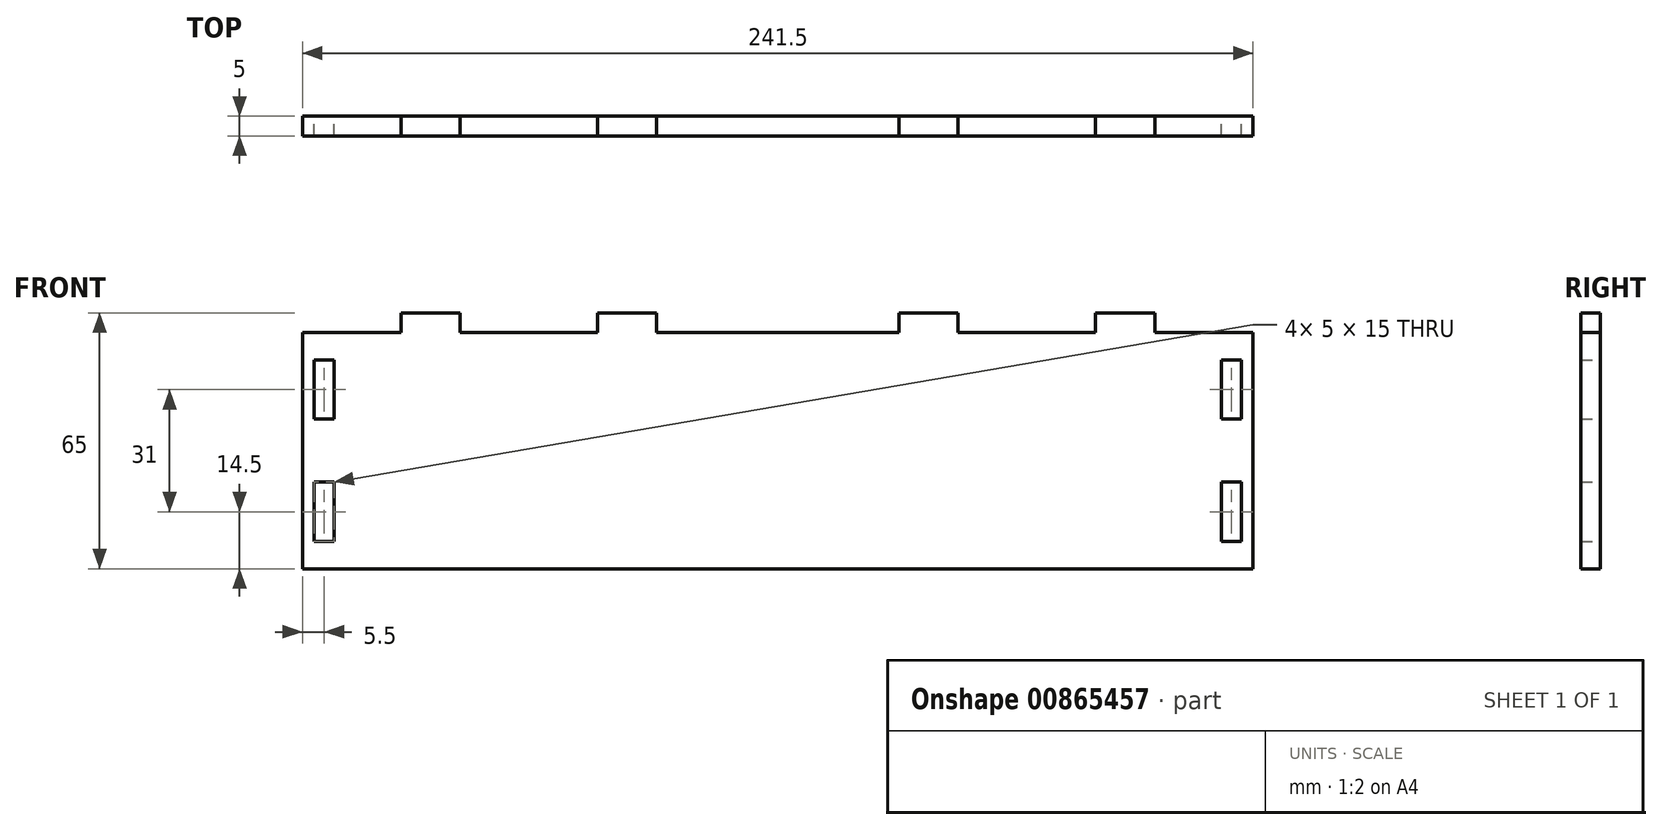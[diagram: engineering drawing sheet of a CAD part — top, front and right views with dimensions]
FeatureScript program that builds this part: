
annotation { "Feature Type Name" : "Feature", "Feature Type Description" : "" }
export const myFeature = defineFeature(function(context is Context, id is Id, definition is map)
    precondition{}
    {
        {
            var Q0;
            Q0=qCreatedBy(makeId("Front.planeOp"),FACE);
            var sketch = newSketch(context, id + "F0", { "sketchPlane" : qUnion([Q0])});
            skLineSegment(sketch, "E0.bottom", {"start": v(120.75, -30) * mm, "end": v(-120.75, -30) * mm});
            skLineSegment(sketch, "E0.top", {"start": v(120.75, 30) * mm, "end": v(-120.75, 30) * mm});
            skLineSegment(sketch, "E0.left", {"start": v(120.75, -30) * mm, "end": v(120.75, 30) * mm});
            skLineSegment(sketch, "E0.right", {"start": v(-120.75, -30) * mm, "end": v(-120.75, 30) * mm});
            skPoint(sketch, "E0.middle", {"position": v(0, 0) * mm});
            skLineSegment(sketch, "E1", {"start": v(-95.75, 30) * mm, "end": v(-95.75, 35) * mm});
            skLineSegment(sketch, "E2", {"start": v(-95.75, 35) * mm, "end": v(-80.75, 35) * mm});
            skLineSegment(sketch, "E3", {"start": v(-80.75, 35) * mm, "end": v(-80.75, 30) * mm});
            skSolve(sketch);
        }
        {
            var Q0;
            Q0=qCreatedBy(makeId("Front.planeOp"),FACE);
            var sketch = newSketch(context, id + "F1", { "sketchPlane" : qUnion([Q0])});
            skLineSegment(sketch, "E4.bottom", {"start": v(120.75, -30) * mm, "end": v(-120.75, -30) * mm});
            skLineSegment(sketch, "E4.top", {"start": v(120.75, 30) * mm, "end": v(-30.75, 30) * mm});
            skLineSegment(sketch, "E4.left", {"start": v(120.75, -30) * mm, "end": v(120.75, 30) * mm});
            skLineSegment(sketch, "E4.right", {"start": v(-120.75, -30) * mm, "end": v(-120.75, 30) * mm});
            skPoint(sketch, "E4.middle", {"position": v(0, 0) * mm});
            skLineSegment(sketch, "E5", {"start": v(-95.75, 30) * mm, "end": v(-95.75, 35) * mm});
            skLineSegment(sketch, "E6", {"start": v(-95.75, 35) * mm, "end": v(-80.75, 35) * mm});
            skLineSegment(sketch, "E7", {"start": v(-80.75, 35) * mm, "end": v(-80.75, 30) * mm});
            skLineSegment(sketch, "E8", {"start": v(-45.75, 30) * mm, "end": v(-45.75, 35) * mm});
            skLineSegment(sketch, "E9", {"start": v(-45.75, 35) * mm, "end": v(-30.75, 35) * mm});
            skLineSegment(sketch, "E10", {"start": v(-30.75, 35) * mm, "end": v(-30.75, 30) * mm});
            skLineSegment(sketch, "E11.trimOffspring", {"start": v(-95.75, 30) * mm, "end": v(-120.75, 30) * mm});
            skLineSegment(sketch, "E12.trimOffspring", {"start": v(-45.75, 30) * mm, "end": v(-80.75, 30) * mm});
            skLineSegment(sketch, "E13.MirrorCS", {"start": v(45.75, 35) * mm, "end": v(30.75, 35) * mm});
            skLineSegment(sketch, "E14.MirrorCS", {"start": v(45.75, 30) * mm, "end": v(45.75, 35) * mm});
            skLineSegment(sketch, "E15.MirrorCS", {"start": v(30.75, 35) * mm, "end": v(30.75, 30) * mm});
            skLineSegment(sketch, "E16.MirrorCS", {"start": v(80.75, 35) * mm, "end": v(80.75, 30) * mm});
            skLineSegment(sketch, "E17.MirrorCS", {"start": v(95.75, 30) * mm, "end": v(95.75, 35) * mm});
            skLineSegment(sketch, "E18.MirrorCS", {"start": v(95.75, 35) * mm, "end": v(80.75, 35) * mm});
            skLineSegment(sketch, "E19.bottom", {"start": v(-112.75, 8) * mm, "end": v(-117.75, 8) * mm});
            skLineSegment(sketch, "E19.top", {"start": v(-112.75, 23) * mm, "end": v(-117.75, 23) * mm});
            skLineSegment(sketch, "E19.left", {"start": v(-112.75, 8) * mm, "end": v(-112.75, 23) * mm});
            skLineSegment(sketch, "E19.right", {"start": v(-117.75, 8) * mm, "end": v(-117.75, 23) * mm});
            skPoint(sketch, "E19.middle", {"position": v(-115.25, 15.5) * mm});
            skLineSegment(sketch, "E20.MirrorCS", {"start": v(-117.75, -8) * mm, "end": v(-117.75, -23) * mm});
            skLineSegment(sketch, "E21.MirrorCS", {"start": v(-112.75, -8) * mm, "end": v(-112.75, -23) * mm});
            skLineSegment(sketch, "E22.MirrorCS", {"start": v(-112.75, -23) * mm, "end": v(-117.75, -23) * mm});
            skLineSegment(sketch, "E23.MirrorCS", {"start": v(-112.75, -8) * mm, "end": v(-117.75, -8) * mm});
            skLineSegment(sketch, "E24.MirrorCS", {"start": v(112.75, 8) * mm, "end": v(112.75, 23) * mm});
            skLineSegment(sketch, "E25.MirrorCS", {"start": v(117.75, 8) * mm, "end": v(117.75, 23) * mm});
            skLineSegment(sketch, "E26.MirrorCS", {"start": v(112.75, 23) * mm, "end": v(117.75, 23) * mm});
            skLineSegment(sketch, "E27.MirrorCS", {"start": v(112.75, 8) * mm, "end": v(117.75, 8) * mm});
            skLineSegment(sketch, "E28.MirrorCS", {"start": v(112.75, -8) * mm, "end": v(117.75, -8) * mm});
            skLineSegment(sketch, "E29.MirrorCS", {"start": v(112.75, -8) * mm, "end": v(112.75, -23) * mm});
            skLineSegment(sketch, "E30.MirrorCS", {"start": v(117.75, -8) * mm, "end": v(117.75, -23) * mm});
            skLineSegment(sketch, "E31.MirrorCS", {"start": v(112.75, -23) * mm, "end": v(117.75, -23) * mm});
            skPoint(sketch, "E32.middle", {"position": v(80.75, -8.68) * mm});
            skSolve(sketch);
        }
        {
            var Q0;
            Q0=makeQuery(id+"F1.imprint","IMPRINT",FACE,{"disambiguationData":[TD([[makeQuery(id+"F1.imprint","IMPRINT",EDGE,{"derivedFrom":sQuery(id+"F1.wireOp",EDGE,"E4.bottom")}),-1.0]])]});
            var Q1;
            Q1=makeQuery(id+"F1.imprint","IMPRINT",FACE,{"disambiguationData":[TD([[makeQuery(id+"F1.imprint","IMPRINT",EDGE,{"derivedFrom":sQuery(id+"F1.wireOp",EDGE,"E13.MirrorCS")}),1.0]])]});
            var Q2;
            {var subQ0=sQuery(id+"F1.wireOp",EDGE,"E16.MirrorCS");Q2=makeQuery(id+"F1.imprint","IMPRINT",FACE,{"disambiguationData":[TD([[makeQuery(id+"F1.imprint","IMPRINT",EDGE,{"derivedFrom":subQ0}),1.0]])]});}
            extrude(context, id + "F2", {"entities" : qUnion([Q0, Q1, Q2]), "depth" : 5 * mm, "offsetDistance" : 25 * mm});
        }
    });
